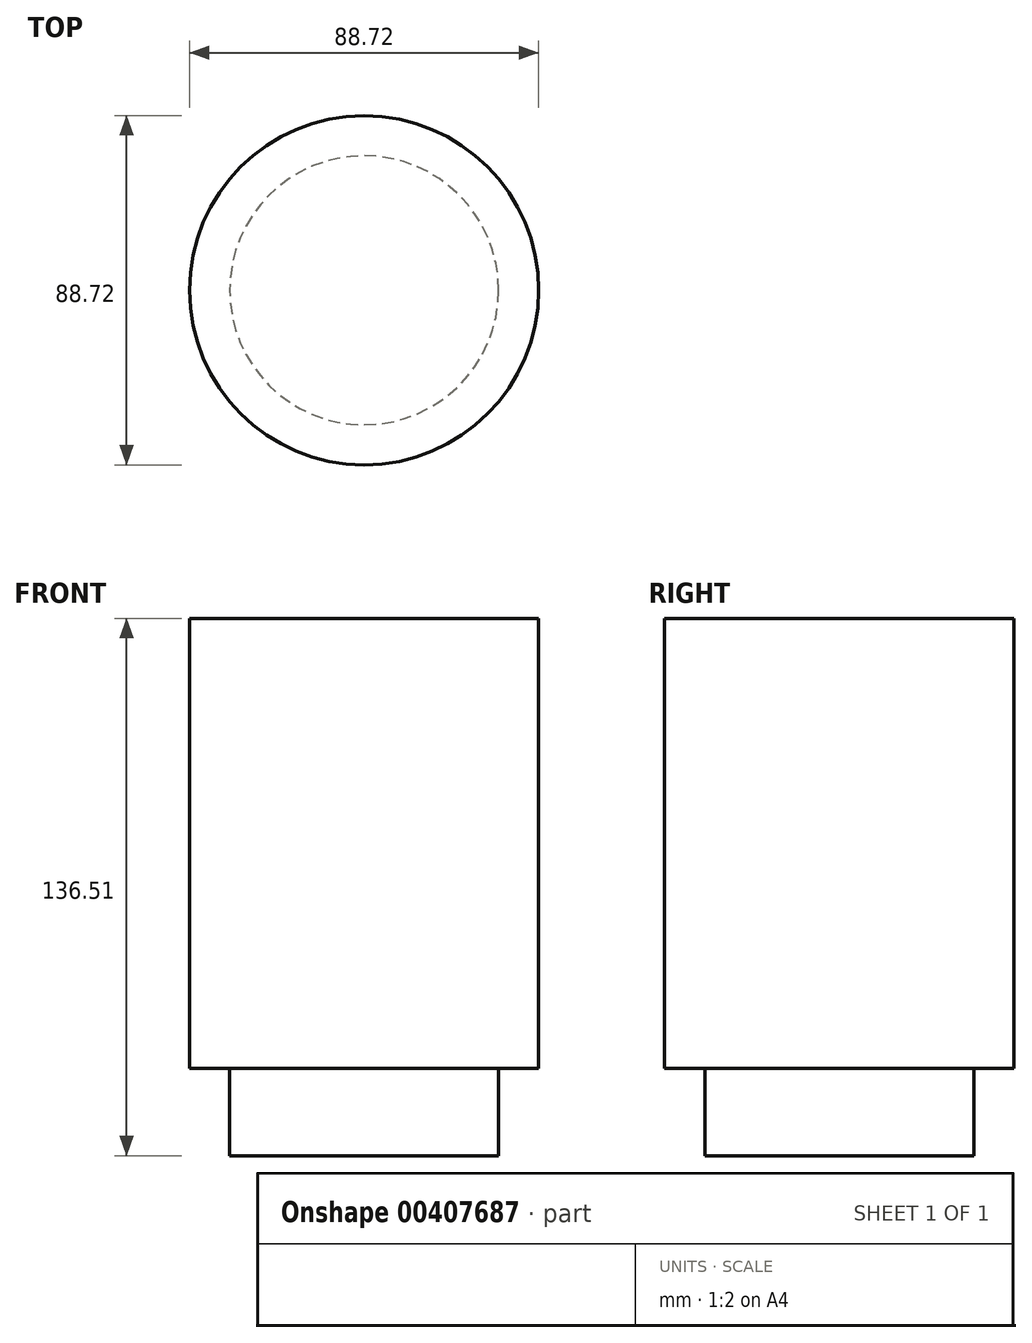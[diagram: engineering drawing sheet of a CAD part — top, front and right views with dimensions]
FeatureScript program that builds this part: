
annotation { "Feature Type Name" : "Feature", "Feature Type Description" : "" }
export const myFeature = defineFeature(function(context is Context, id is Id, definition is map)
    precondition{}
    {
        {
            var Q0;
            Q0=qCreatedBy(makeId("Top.planeOp"),FACE);
            var sketch = newSketch(context, id + "F0", { "sketchPlane" : qUnion([Q0])});
            skCircle(sketch, "E0", {"center": v(0, 0) * mm, "radius": 44.36 * mm});
            skSolve(sketch);
        }
        {
            var Q0;
            Q0=makeQuery(id+"F0.imprint","IMPRINT",FACE,{"disambiguationData":[TD([[makeQuery(id+"F0.imprint","IMPRINT",EDGE,{"derivedFrom":sQuery(id+"F0.wireOp",EDGE,"E0")}),1.0]])]});
            extrude(context, id + "F1", {"entities" : qUnion([Q0]), "depth" : 114.3 * mm});
        }
        {
            var Q0;
            Q0=makeQuery(id+"F1.opExtrude","CAP_FACE",FACE,{"disambiguationData":[OSD([sQuery(id+"F0.wireOp",EDGE,"E0")])],"isStart":true});
            var sketch = newSketch(context, id + "F2", { "sketchPlane" : qUnion([Q0])});
            skCircle(sketch, "E1", {"center": v(0, 0) * mm, "radius": 34.17 * mm});
            skSolve(sketch);
        }
        {
            var Q0;
            Q0 = qSketchRegion(id + "F2", true);
            extrude(context, id + "F3", {"entities" : qUnion([Q0]), "operationType" : NewBodyOperationType.ADD, "depth" : 10.16 * mm});
        }
        {
            var Q0;
            Q0=makeQuery(id+"F3.opExtrude","CAP_FACE",FACE,{"disambiguationData":[OSD([sQuery(id+"F2.wireOp",EDGE,"E1")])],"isStart":false});
            var sketch = newSketch(context, id + "F4", { "sketchPlane" : qUnion([Q0])});
            skCircle(sketch, "E2", {"center": v(0, 0) * mm, "radius": 38.13 * mm});
            skSolve(sketch);
        }
        {
            var Q0;
            Q0=makeQuery(id+"F4.imprint","IMPRINT",FACE,{"disambiguationData":[TD([[makeQuery(id+"F4.imprint","IMPRINT",EDGE,{"derivedFrom":makeQuery(id+"F3.opExtrude","CAP_EDGE",EDGE,{"disambiguationData":[OSD([sQuery(id+"F2.wireOp",EDGE,"E1")])],"isStart":false})}),1.0]])]});
            extrude(context, id + "F5", {"entities" : qUnion([Q0]), "operationType" : NewBodyOperationType.ADD, "depth" : 12.05 * mm});
        }
    });
